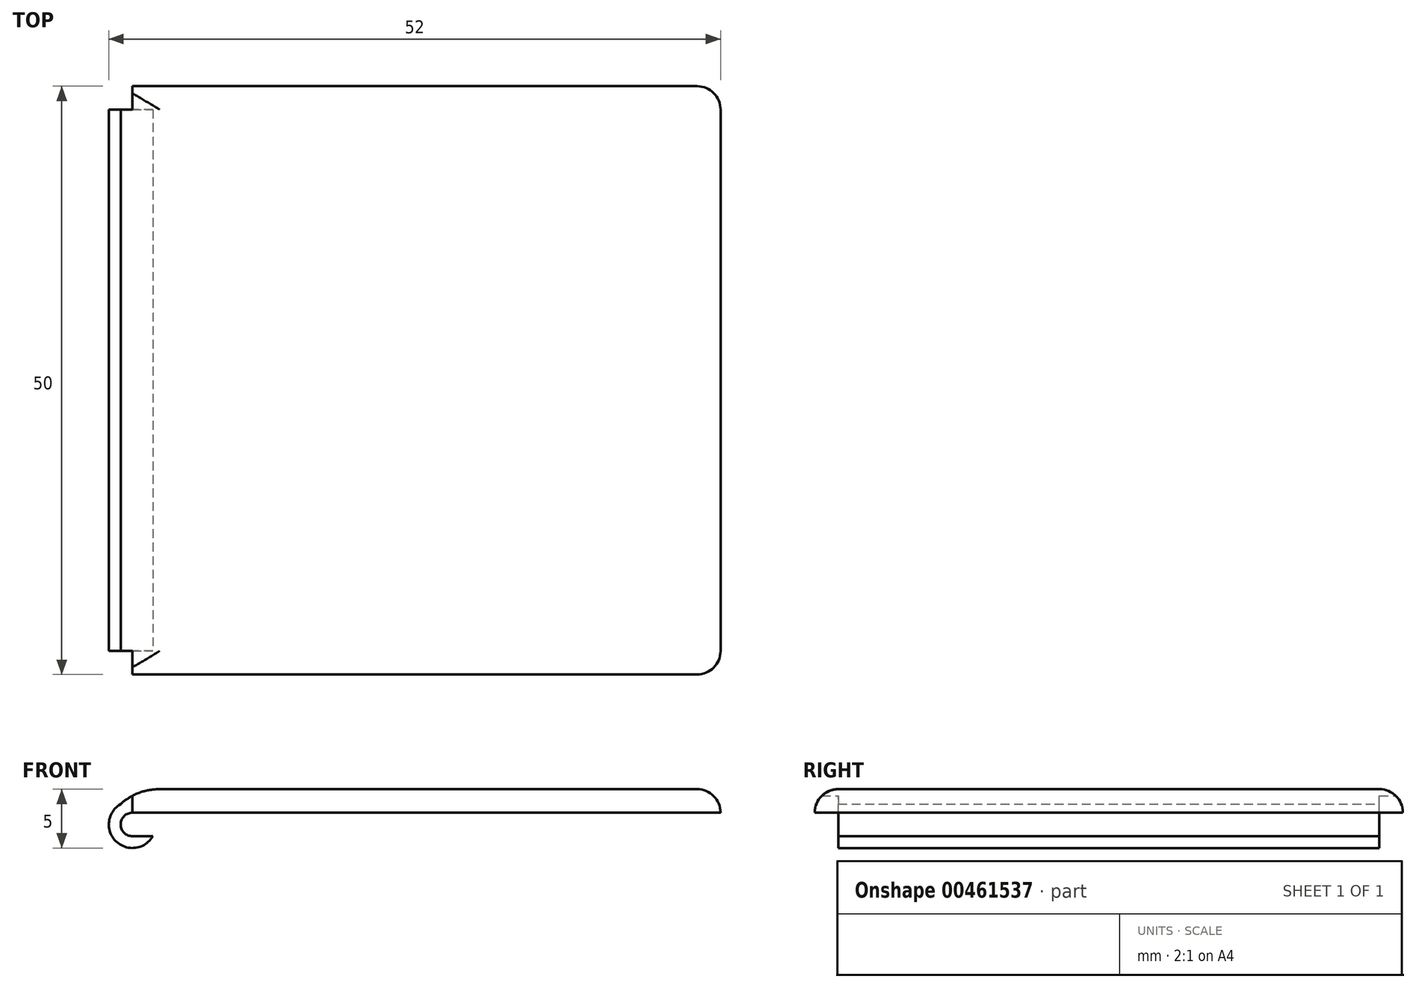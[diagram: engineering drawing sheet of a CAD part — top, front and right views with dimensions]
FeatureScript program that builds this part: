
annotation { "Feature Type Name" : "Feature", "Feature Type Description" : "" }
export const myFeature = defineFeature(function(context is Context, id is Id, definition is map)
    precondition{}
    {
        {
            var Q0;
            Q0=qCreatedBy(makeId("Top.planeOp"),FACE);
            var sketch = newSketch(context, id + "F0", { "sketchPlane" : qUnion([Q0])});
            skLineSegment(sketch, "E0.bottom", {"start": v(-14.72, 26.04) * mm, "end": v(35.28, 26.04) * mm});
            skLineSegment(sketch, "E0.top", {"start": v(-14.72, -23.96) * mm, "end": v(35.28, -23.96) * mm});
            skLineSegment(sketch, "E0.left", {"start": v(-14.72, 26.04) * mm, "end": v(-14.72, -23.96) * mm});
            skLineSegment(sketch, "E0.right", {"start": v(35.28, 26.04) * mm, "end": v(35.28, -23.96) * mm});
            skSolve(sketch);
        }
        {
            var Q0;
            Q0=makeQuery(id+"F0.imprint","IMPRINT",FACE,{"disambiguationData":[TD([[makeQuery(id+"F0.imprint","IMPRINT",EDGE,{"derivedFrom":sQuery(id+"F0.wireOp",EDGE,"E0.bottom")}),-1.0]])]});
            extrude(context, id + "F1", {"entities" : qUnion([Q0]), "depth" : 2 * mm});
        }
        {
            var Q0;
            Q0=makeQuery(id+"F1.opExtrude","SWEPT_FACE",FACE,{"disambiguationData":[OSD([sQuery(id+"F0.wireOp",EDGE,"E0.left")])]});
            var sketch = newSketch(context, id + "F2", { "sketchPlane" : qUnion([Q0])});
            skLineSegment(sketch, "E1", {"start": v(23.96, 0) * mm, "end": v(21.96, 0) * mm});
            skLineSegment(sketch, "E2", {"start": v(21.96, 0) * mm, "end": v(21.96, -1) * mm});
            skLineSegment(sketch, "E3", {"start": v(21.96, 0) * mm, "end": v(21.96, 1.43) * mm});
            skLineSegment(sketch, "E4.top", {"start": v(23.96, -1) * mm, "end": v(21.96, -1) * mm});
            skLineSegment(sketch, "E4.left", {"start": v(23.96, 0) * mm, "end": v(23.96, -1) * mm});
            skSolve(sketch);
        }
        {
            var Q0;
            Q0=makeQuery(id+"F2.imprint","IMPRINT",FACE,{"disambiguationData":[TD([[makeQuery(id+"F2.imprint","IMPRINT",EDGE,{"derivedFrom":sQuery(id+"F2.wireOp",EDGE,"E1")}),-1.0]])]});
            extrude(context, id + "F3", {"entities" : qUnion([Q0]), "oppositeDirection" : true, "depth" : 25 * mm});
        }
        {
            var Q0;
            Q0=makeQuery(id+"F3.opExtrude","SWEPT_FACE",FACE,{"disambiguationData":[OSD([sQuery(id+"F2.wireOp",EDGE,"E2")])]});
            var sketch = newSketch(context, id + "F4", { "sketchPlane" : qUnion([Q0])});
            skCircle(sketch, "E5", {"center": v(14.72, -1) * mm, "radius": 1 * mm});
            skCircle(sketch, "E6", {"center": v(14.72, -1) * mm, "radius": 2 * mm});
            skSolve(sketch);
        }
        {
            var Q0;
            {var subQ1=sQuery(id+"F2.wireOp",EDGE,"E2");var subQ4=makeQuery(id+"F3.opExtrude","SWEPT_EDGE",EDGE,{"disambiguationData":[OSD([sQuery(id+"F2.wireOp",EDGE,"E4.top"),subQ1])]});var subQ6=sQuery(id+"F4.wireOp",EDGE,"E6");var subQ8=makeQuery(id+"F4.imprint","INTERSECT",VERTEX,{"derivedFrom":[subQ4,subQ6]});Q0=makeQuery(id+"F4.imprint","IMPRINT",FACE,{"disambiguationData":[TD([[makeQuery(id+"F4.imprint","IMPRINT",EDGE,{"disambiguationData":[TD([[subQ8,-1.0]])],"derivedFrom":subQ6}),1.0]])]});}
            var Q1;
            {var subQ1=sQuery(id+"F2.wireOp",EDGE,"E2");var subQ4=makeQuery(id+"F3.opExtrude","SWEPT_EDGE",EDGE,{"disambiguationData":[OSD([sQuery(id+"F2.wireOp",EDGE,"E4.top"),subQ1])]});var subQ6=sQuery(id+"F4.wireOp",EDGE,"E6");var subQ7=makeQuery(id+"F4.imprint","INTERSECT",VERTEX,{"derivedFrom":[subQ4,subQ6]});Q1=makeQuery(id+"F4.imprint","IMPRINT",FACE,{"disambiguationData":[TD([[makeQuery(id+"F4.imprint","IMPRINT",EDGE,{"disambiguationData":[TD([[subQ7,1.0]])],"derivedFrom":subQ6}),1.0]])]});}
            extrude(context, id + "F5", {"entities" : qUnion([Q0, Q1]), "depth" : 46 * mm});
        }
        {
            var Q0;
            Q0=makeQuery(id+"F3.opExtrude","CAP_FACE",FACE,{"disambiguationData":[OSD([sQuery(id+"F2.wireOp",EDGE,"E1"),sQuery(id+"F2.wireOp",EDGE,"E4.top"),sQuery(id+"F2.wireOp",EDGE,"E4.left"),sQuery(id+"F2.wireOp",EDGE,"E2")])],"isStart":true});
            extrude(context, id + "F6", {"entities" : qUnion([Q0]), "operationType" : NewBodyOperationType.REMOVE, "oppositeDirection" : true, "depth" : 25 * mm});
        }
        {
            var Q0;
            Q0=makeQuery(id+"F5.opExtrude","CAP_FACE",FACE,{"disambiguationData":[OSD([sQuery(id+"F4.wireOp",EDGE,"E5"),sQuery(id+"F4.wireOp",EDGE,"E6")])],"isStart":true});
            var sketch = newSketch(context, id + "F7", { "sketchPlane" : qUnion([Q0])});
            skLineSegment(sketch, "E7", {"start": v(-14.72, -1) * mm, "end": v(-14.72, -2) * mm});
            skLineSegment(sketch, "E8", {"start": v(-14.72, -2) * mm, "end": v(-14.72, 0) * mm});
            skLineSegment(sketch, "E9", {"start": v(-14.72, 0) * mm, "end": v(-12.98, 0) * mm});
            skLineSegment(sketch, "E10", {"start": v(-14.72, -2) * mm, "end": v(-12.98, -2) * mm});
            skSolve(sketch);
        }
        {
            var Q0;
            Q0 = qSketchRegion(id + "F7", true);
            var Q1;
            {var subQ0=sQuery(id+"F7.wireOp",EDGE,"E9");Q1=makeQuery(id+"F7.imprint","IMPRINT",FACE,{"disambiguationData":[TD([[makeQuery(id+"F7.imprint","IMPRINT",EDGE,{"derivedFrom":subQ0}),-1.0]])]});}
            extrude(context, id + "F8", {"entities" : qUnion([Q0, Q1]), "operationType" : NewBodyOperationType.REMOVE, "oppositeDirection" : true, "depth" : 46 * mm});
        }
        {
            var Q0;
            Q0=makeQuery(id+"F5.opExtrude","CAP_FACE",FACE,{"disambiguationData":[OSD([sQuery(id+"F4.wireOp",EDGE,"E5"),sQuery(id+"F4.wireOp",EDGE,"E6")])],"isStart":true});
            var sketch = newSketch(context, id + "F9", { "sketchPlane" : qUnion([Q0])});
            skLineSegment(sketch, "E11.bottom", {"start": v(-14.72, 0) * mm, "end": v(-15.72, 0) * mm});
            skLineSegment(sketch, "E11.top", {"start": v(-14.72, 2) * mm, "end": v(-15.72, 2) * mm});
            skLineSegment(sketch, "E11.left", {"start": v(-14.72, 0) * mm, "end": v(-14.72, 2) * mm});
            skLineSegment(sketch, "E11.right", {"start": v(-15.72, 0) * mm, "end": v(-15.72, 2) * mm});
            skSolve(sketch);
        }
        {
            var Q0;
            {var subQ0=sQuery(id+"F9.wireOp",EDGE,"E11.top");Q0=makeQuery(id+"F9.imprint","IMPRINT",FACE,{"disambiguationData":[TD([[makeQuery(id+"F9.imprint","IMPRINT",EDGE,{"derivedFrom":subQ0}),1.0]])]});}
            extrude(context, id + "F10", {"entities" : qUnion([Q0]), "operationType" : NewBodyOperationType.ADD, "oppositeDirection" : true, "depth" : 46 * mm});
        }
        {
            var Q0;
            Q0=makeQuery(id+"F10.opExtrude","SWEPT_EDGE",EDGE,{"disambiguationData":[OSD([sQuery(id+"F9.wireOp",EDGE,"E11.top"),sQuery(id+"F9.wireOp",EDGE,"E11.right")])]});
            fillet(context, id + "F11", {"entities" : qUnion([Q0]), "radius" : 5 * mm, "rho" : 0.5, "crossSection" : FilletCrossSection.CONIC, "allowEdgeOverflow" : false});
        }
        {
            var Q0;
            Q0=makeQuery(id+"F1.opExtrude","CAP_EDGE",EDGE,{"disambiguationData":[OSD([sQuery(id+"F0.wireOp",EDGE,"E0.top")])],"isStart":false});
            var Q1;
            Q1=makeQuery(id+"F1.opExtrude","CAP_EDGE",EDGE,{"disambiguationData":[OSD([sQuery(id+"F0.wireOp",EDGE,"E0.right")])],"isStart":false});
            var Q2;
            Q2=makeQuery(id+"F1.opExtrude","CAP_EDGE",EDGE,{"disambiguationData":[OSD([sQuery(id+"F0.wireOp",EDGE,"E0.bottom")])],"isStart":false});
            fillet(context, id + "F12", {"entities" : qUnion([Q0, Q1, Q2]), "radius" : 2 * mm, "tangentPropagation" : true, "allowEdgeOverflow" : false});
        }
        {
            var Q0;
            Q0=makeQuery(id+"F12.opFillet","BLEND_EDGE",EDGE,{"blendedFrom":[makeQuery(id+"F1.opExtrude","CAP_EDGE",EDGE,{"disambiguationData":[OSD([sQuery(id+"F0.wireOp",EDGE,"E0.top")])],"isStart":false}),makeQuery(id+"F1.opExtrude","CAP_EDGE",EDGE,{"disambiguationData":[OSD([sQuery(id+"F0.wireOp",EDGE,"E0.right")])],"isStart":false})],"blendedInto":[]});
            var Q1;
            Q1=makeQuery(id+"F12.opFillet","BLEND_EDGE",EDGE,{"blendedFrom":[makeQuery(id+"F1.opExtrude","CAP_EDGE",EDGE,{"disambiguationData":[OSD([sQuery(id+"F0.wireOp",EDGE,"E0.bottom")])],"isStart":false}),makeQuery(id+"F1.opExtrude","CAP_EDGE",EDGE,{"disambiguationData":[OSD([sQuery(id+"F0.wireOp",EDGE,"E0.right")])],"isStart":false})],"blendedInto":[]});
            fillet(context, id + "F13", {"entities" : qUnion([Q0, Q1]), "radius" : 2 * mm, "tangentPropagation" : true, "allowEdgeOverflow" : false});
        }
    });
